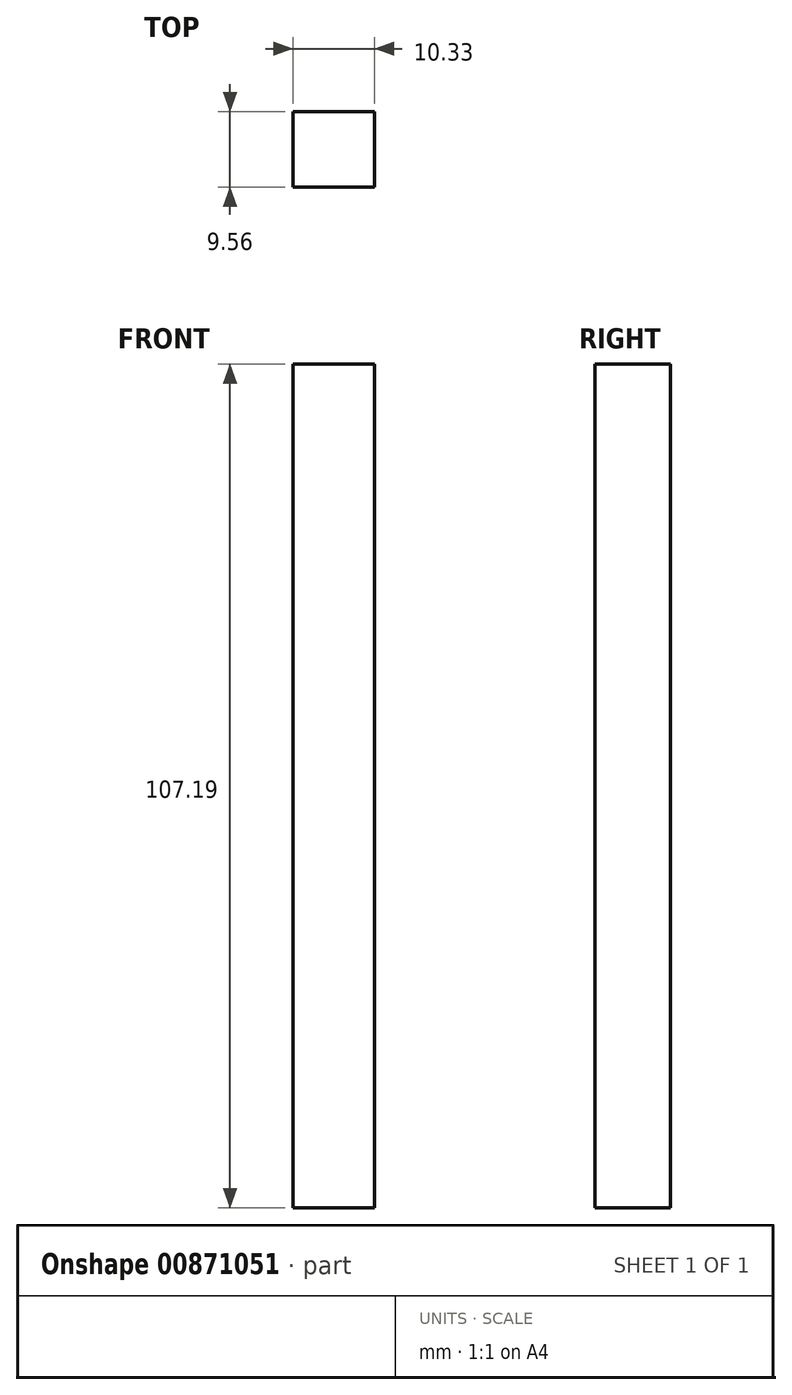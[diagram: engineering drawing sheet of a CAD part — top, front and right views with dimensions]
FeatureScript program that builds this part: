
annotation { "Feature Type Name" : "Feature", "Feature Type Description" : "" }
export const myFeature = defineFeature(function(context is Context, id is Id, definition is map)
    precondition{}
    {
        {
            var Q0;
            Q0=qCreatedBy(makeId("Top.planeOp"),FACE);
            var sketch = newSketch(context, id + "F0", { "sketchPlane" : qUnion([Q0])});
            skLineSegment(sketch, "E0.bottom", {"start": v(0, 0) * mm, "end": v(-10.33, 0) * mm});
            skLineSegment(sketch, "E0.top", {"start": v(0, 9.56) * mm, "end": v(-10.33, 9.56) * mm});
            skLineSegment(sketch, "E0.left", {"start": v(0, 0) * mm, "end": v(0, 9.56) * mm});
            skLineSegment(sketch, "E0.right", {"start": v(-10.33, 0) * mm, "end": v(-10.33, 9.56) * mm});
            skSolve(sketch);
        }
        {
            var Q0;
            Q0=makeQuery(id+"F0.imprint","IMPRINT",FACE,{"disambiguationData":[TD([[makeQuery(id+"F0.imprint","IMPRINT",EDGE,{"derivedFrom":sQuery(id+"F0.wireOp",EDGE,"E0.bottom")}),-1.0]])]});
            extrude(context, id + "F1", {"entities" : qUnion([Q0]), "depth" : 107.19 * mm, "offsetDistance" : 25.4 * mm});
        }
    });
